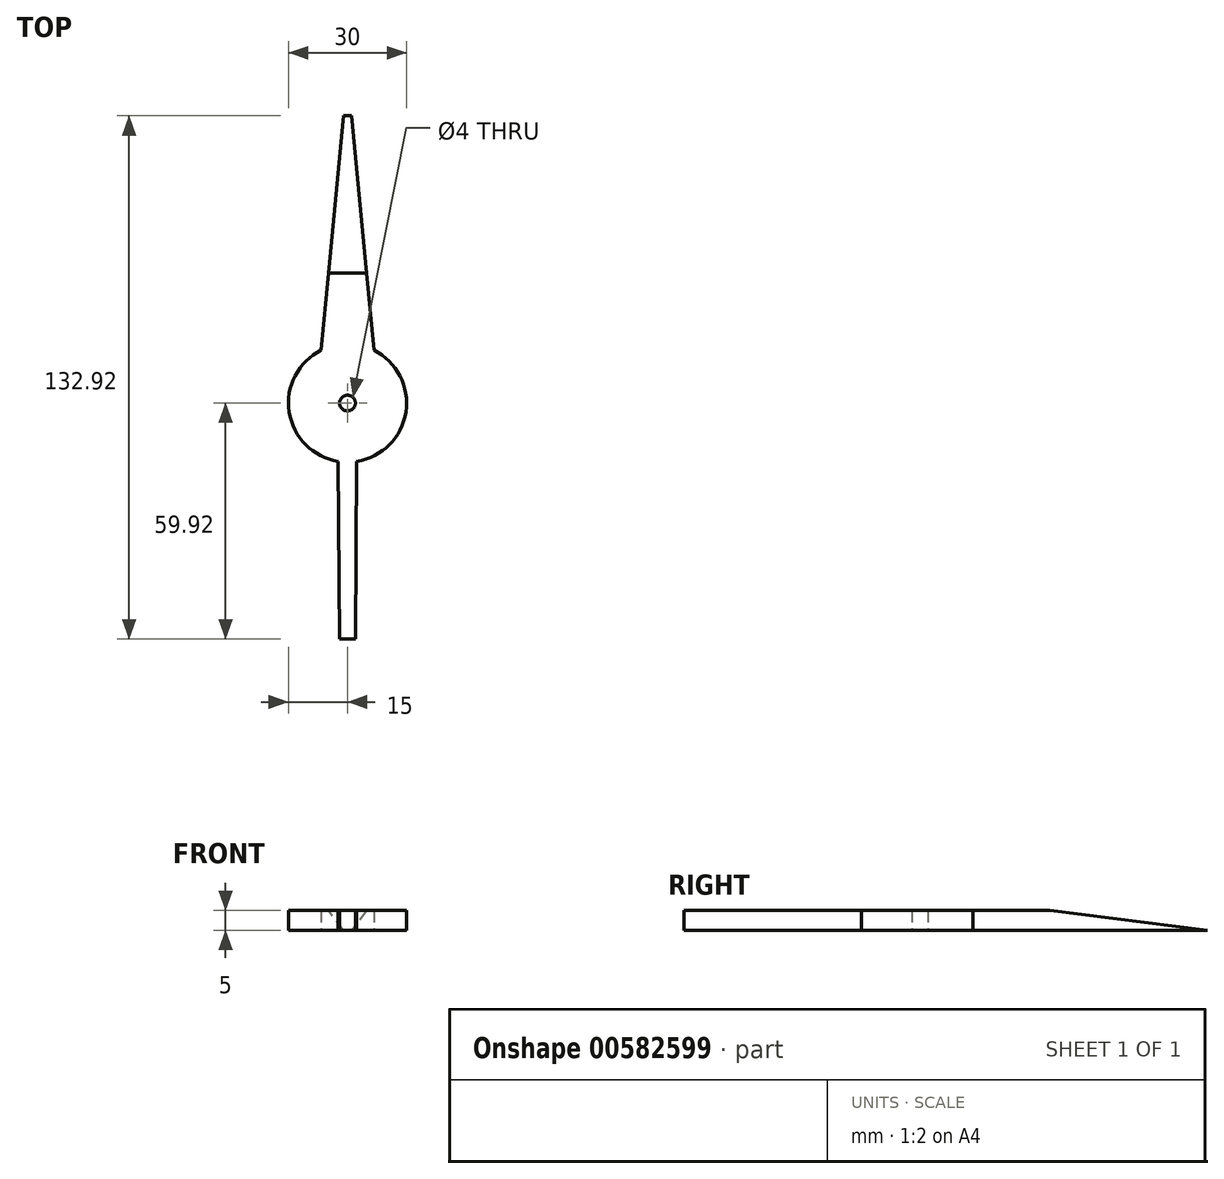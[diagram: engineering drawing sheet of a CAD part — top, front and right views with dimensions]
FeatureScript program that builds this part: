
annotation { "Feature Type Name" : "Feature", "Feature Type Description" : "" }
export const myFeature = defineFeature(function(context is Context, id is Id, definition is map)
    precondition{}
    {
        {
            var Q0;
            Q0=qCreatedBy(makeId("Top.planeOp"),FACE);
            var sketch = newSketch(context, id + "F0", { "sketchPlane" : qUnion([Q0])});
            skLineSegment(sketch, "E0", {"start": v(0, 79.3) * mm, "end": v(0, -90.64) * mm, "construction": true});
            skLineSegment(sketch, "E1", {"start": v(0, 73) * mm, "end": v(1, 73) * mm});
            skLineSegment(sketch, "E2", {"start": v(1, 73) * mm, "end": v(6.7, 13.43) * mm});
            skLineSegment(sketch, "E3", {"start": v(6.7, 13.43) * mm, "end": v(2.36, -14.81) * mm});
            skLineSegment(sketch, "E4", {"start": v(2.36, -14.81) * mm, "end": v(2, -59.92) * mm});
            skLineSegment(sketch, "E5", {"start": v(2, -59.92) * mm, "end": v(0, -59.92) * mm});
            skCircle(sketch, "E6", {"center": v(0, 0) * mm, "radius": 15 * mm});
            skLineSegment(sketch, "E7.MirrorCS", {"start": v(-1, 73) * mm, "end": v(-6.7, 13.43) * mm});
            skLineSegment(sketch, "E8.MirrorCS", {"start": v(-6.7, 13.43) * mm, "end": v(-2.36, -14.81) * mm});
            skLineSegment(sketch, "E9.MirrorCS", {"start": v(-2.36, -14.81) * mm, "end": v(-2, -59.92) * mm});
            skLineSegment(sketch, "E10.MirrorCS", {"start": v(-2, -59.92) * mm, "end": v(0, -59.92) * mm});
            skLineSegment(sketch, "E11.MirrorCS", {"start": v(0, 73) * mm, "end": v(-1, 73) * mm});
            skCircle(sketch, "E12", {"center": v(0, 0) * mm, "radius": 2 * mm});
            skSolve(sketch);
        }
        {
            var Q0;
            Q0 = qSketchRegion(id + "F0", true);
            extrude(context, id + "F1", {"entities" : qUnion([Q0]), "depth" : 5 * mm, "offsetDistance" : 25 * mm});
        }
        {
            var Q0;
            Q0=makeQuery(id+"F1.opExtrude","CAP_EDGE",EDGE,{"disambiguationData":[OSD([sQuery(id+"F0.wireOp",EDGE,"E1"),sQuery(id+"F0.wireOp",EDGE,"E11.MirrorCS")])],"isStart":false});
            chamfer(context, id + "F2", {"entities" : qUnion([Q0]), "chamferType" : ChamferType.TWO_OFFSETS, "width1" : 5 * mm, "oppositeDirection" : false, "width2" : 40 * mm, "tangentPropagation" : true});
        }
    });
